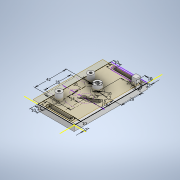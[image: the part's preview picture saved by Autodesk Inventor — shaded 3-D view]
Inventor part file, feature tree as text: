
AUTODESK INVENTOR PART (.ipt)
format: ipt  version: 2022.2 (Build 262287000, 287)  size: 4,157,440 bytes
history: native  units: mm
features: sketch x10, extrude x6, thread x3, revolve x3, helix x3, other x2, hole x1, fillet x1, projected_geometry x1
ambient origin geometry x8: Origin, YZ Plane, XZ Plane, XY Plane, X Axis, Y Axis, Z Axis, Center Point
bodies: Solid2 (feature_tree), Solid3 (feature_tree), Solid4 (feature_tree)
feature tree (30):
  other  "Base Plate"
  sketch  "Sketch1"  dims[d0=10.0mm d1=3.2mm d2=42.0mm d3=8.0mm d4=16.0mm d5=35.0mm d6=35.0mm d7=10.0mm d8=5.2mm d9=7.5mm d10=0.0mm]
  extrude  "Extrusion1"  Depth=10.0mm TaperAngle=0.0deg
  extrude  "Motor Mount"  Depth=3.0mm
  extrude  "Extrusion3"  Depth=11.0mm
  hole  "Hole1"  [1 undecoded]
  extrude  "Extrusion4"  Depth=3.0mm
  extrude  "Extrusion5"  Depth=10.0mm
  thread  "Thread1"  [1 undecoded]
  thread  "Thread2"  [1 undecoded]
  thread  "Thread3"  [1 undecoded]
  other  "Wire Plane"
  fillet  "Fillet1"  Radius=10.0mm
  revolve  "Revolution1"  [1 undecoded]
  helix  "Coil1"  [1 undecoded]
  revolve  "Revolution2"  [1 undecoded]
  helix  "Coil2"  [1 undecoded]
  revolve  "Revolution3"  [1 undecoded]
  helix  "Coil3"  [1 undecoded]
  extrude  "Extrusion6"  Depth=3.0mm
  sketch  "Sketch3"  dims[d11=12.0mm d12=0.0mm d13=3.0mm]
  projected_geometry  "Projected Loop1"
  sketch  "Sketch4"  dims[d14=16.0mm d15=11.0mm]
  sketch  "Sketch5"  dims[d16=14.0mm d17=12.0mm d18=0.0mm]
  sketch  "Sketch6"  dims[d19=3.0mm d20=6.0mm d21=6.0mm d22=2.0mm d23=90.0deg d24=8.0mm d25=0.0mm d26=20.0mm]
  sketch  "Sketch7"  dims[d27=6.0mm d28=6.0mm d29=28.0mm d30=7.0mm d31=2.0mm d32=10.0mm]
  sketch  "Sketch8"  dims[d33=10.0mm d34=1.5mm d35=3.5mm d36=0.0mm]
  sketch  "Sketch9"  dims[d37=10.0mm d38=0.0mm d39=17.5mm d40=0.0mm d41=19.5mm d42=0.0mm]
  sketch  "Sketch10"  dims[d43=19.5mm d44=0.0mm d45=7.0mm d48=2.0mm d49=10.0mm]
  sketch  "Sketch11"  dims[d50=10.0mm d51=1.5mm d52=2.0mm d56=9.599311mm d57=0.128066mm d58=0.128066mm d61=0.8mm d63=9.599311mm d65=0.0mm d66=0.8008mm d67=19.1mm d68=10.0mm d69=0.0mm d70=0.0mm d71=0.0mm d72=0.0mm d73=0.0mm d74=9.599311mm d75=0.080042mm d76=0.080042mm d79=0.5mm d81=9.599311mm d83=0.0mm d84=0.5005mm d85=20.5mm d86=10.0mm d87=0.0mm d88=0.0mm d89=0.0mm d90=0.0mm d91=0.0mm d92=9.599311mm d93=0.080042mm d94=0.080042mm d97=0.5mm d99=9.599311mm d101=0.0mm d102=0.5005mm d103=20.5mm d104=10.0mm d105=0.0mm d106=0.0mm d107=0.0mm d108=0.0mm d109=0.0mm d110=6.0mm d111=13.0mm d112=3.0mm d113=0.0mm]
note: 10 required parameter values undecoded (feature->parameter linkage not recoverable at this tier; creation-order binding heuristic only, values carry confidence <= 0.55)